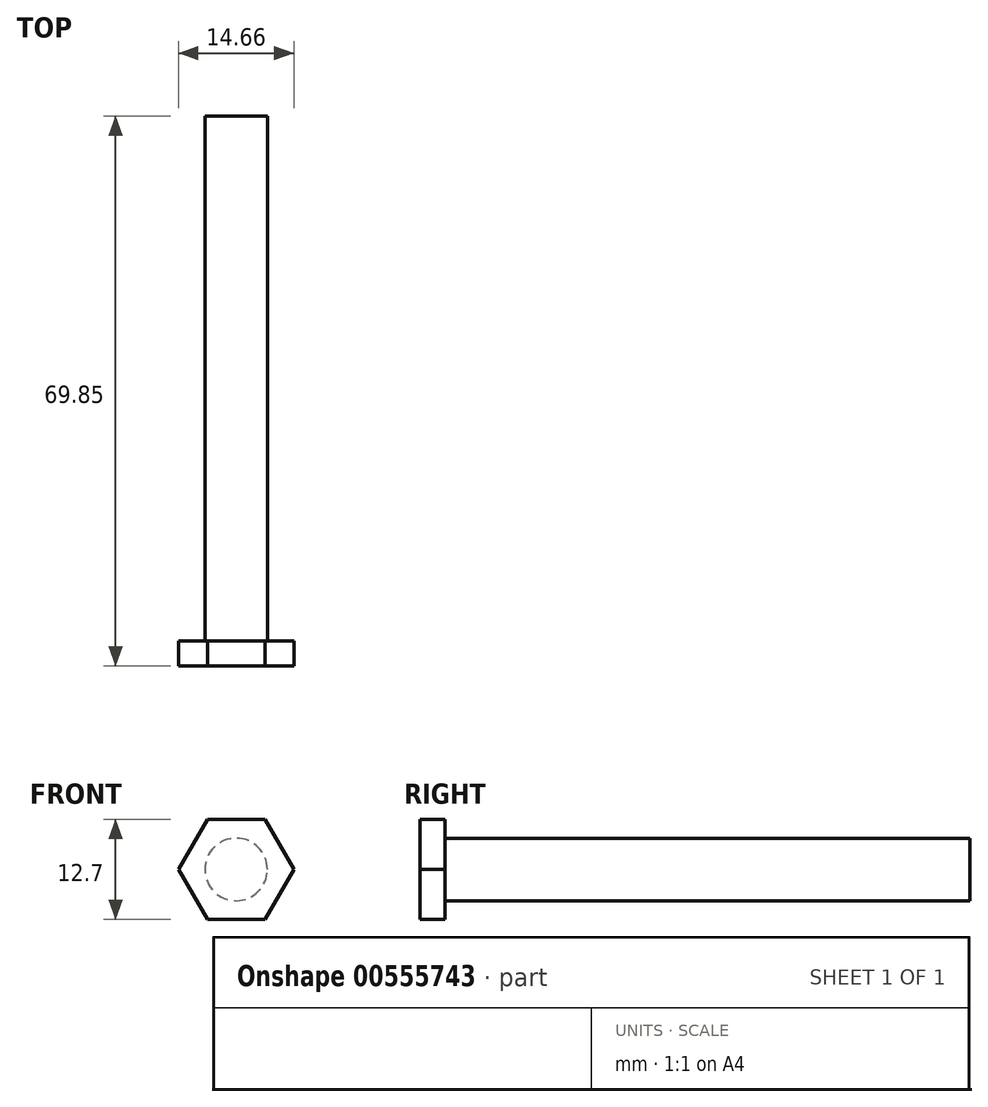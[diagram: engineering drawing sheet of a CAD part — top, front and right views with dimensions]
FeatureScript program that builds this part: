
annotation { "Feature Type Name" : "Feature", "Feature Type Description" : "" }
export const myFeature = defineFeature(function(context is Context, id is Id, definition is map)
    precondition{}
    {
        {
            var Q0;
            Q0=qCreatedBy(makeId("Front.planeOp"),FACE);
            var sketch = newSketch(context, id + "F0", { "sketchPlane" : qUnion([Q0])});
            skCircle(sketch, "E0", {"center": v(0, 0) * mm, "radius": 3.97 * mm});
            skSolve(sketch);
        }
        {
            var Q0;
            Q0=makeQuery(id+"F0.imprint","IMPRINT",FACE,{"disambiguationData":[TD([[makeQuery(id+"F0.imprint","IMPRINT",EDGE,{"derivedFrom":sQuery(id+"F0.wireOp",EDGE,"E0")}),1.0]])]});
            extrude(context, id + "F1", {"entities" : qUnion([Q0]), "depth" : 66.67 * mm, "offsetDistance" : 25.4 * mm});
        }
        {
            var Q0;
            Q0=makeQuery(id+"F1.opExtrude","CAP_FACE",FACE,{"disambiguationData":[OSD([sQuery(id+"F0.wireOp",EDGE,"E0")])],"isStart":false});
            var sketch = newSketch(context, id + "F2", { "sketchPlane" : qUnion([Q0])});
            skCircle(sketch, "E1.cCircle", {"center": v(0, 0) * mm, "radius": 6.35 * mm, "construction": true});
            skLineSegment(sketch, "E1.0", {"start": v(-3.67, 6.35) * mm, "end": v(3.67, 6.35) * mm});
            skLineSegment(sketch, "E1.1", {"start": v(3.67, 6.35) * mm, "end": v(7.33, 0) * mm});
            skLineSegment(sketch, "E1.2", {"start": v(7.33, 0) * mm, "end": v(3.67, -6.35) * mm});
            skLineSegment(sketch, "E1.3", {"start": v(3.67, -6.35) * mm, "end": v(-3.67, -6.35) * mm});
            skLineSegment(sketch, "E1.4", {"start": v(-3.67, -6.35) * mm, "end": v(-7.33, 0) * mm});
            skLineSegment(sketch, "E1.5", {"start": v(-7.33, 0) * mm, "end": v(-3.67, 6.35) * mm});
            skPoint(sketch, "E1.0.midPoint", {"position": v(0, 6.35) * mm});
            skSolve(sketch);
        }
        {
            var Q0;
            Q0=makeQuery(id+"F2.imprint","IMPRINT",FACE,{"disambiguationData":[TD([[makeQuery(id+"F2.imprint","IMPRINT",EDGE,{"derivedFrom":sQuery(id+"F2.wireOp",EDGE,"E1.0")}),-1.0]])]});
            var Q1;
            Q1=makeQuery(id+"F2.imprint","IMPRINT",FACE,{"disambiguationData":[TD([[makeQuery(id+"F2.imprint","IMPRINT",EDGE,{"derivedFrom":makeQuery(id+"F1.opExtrude","CAP_EDGE",EDGE,{"disambiguationData":[OSD([sQuery(id+"F0.wireOp",EDGE,"E0")])],"isStart":false})}),1.0]])]});
            extrude(context, id + "F3", {"entities" : qUnion([Q0, Q1]), "operationType" : NewBodyOperationType.ADD, "depth" : 3.17 * mm, "offsetDistance" : 25.4 * mm});
        }
    });
